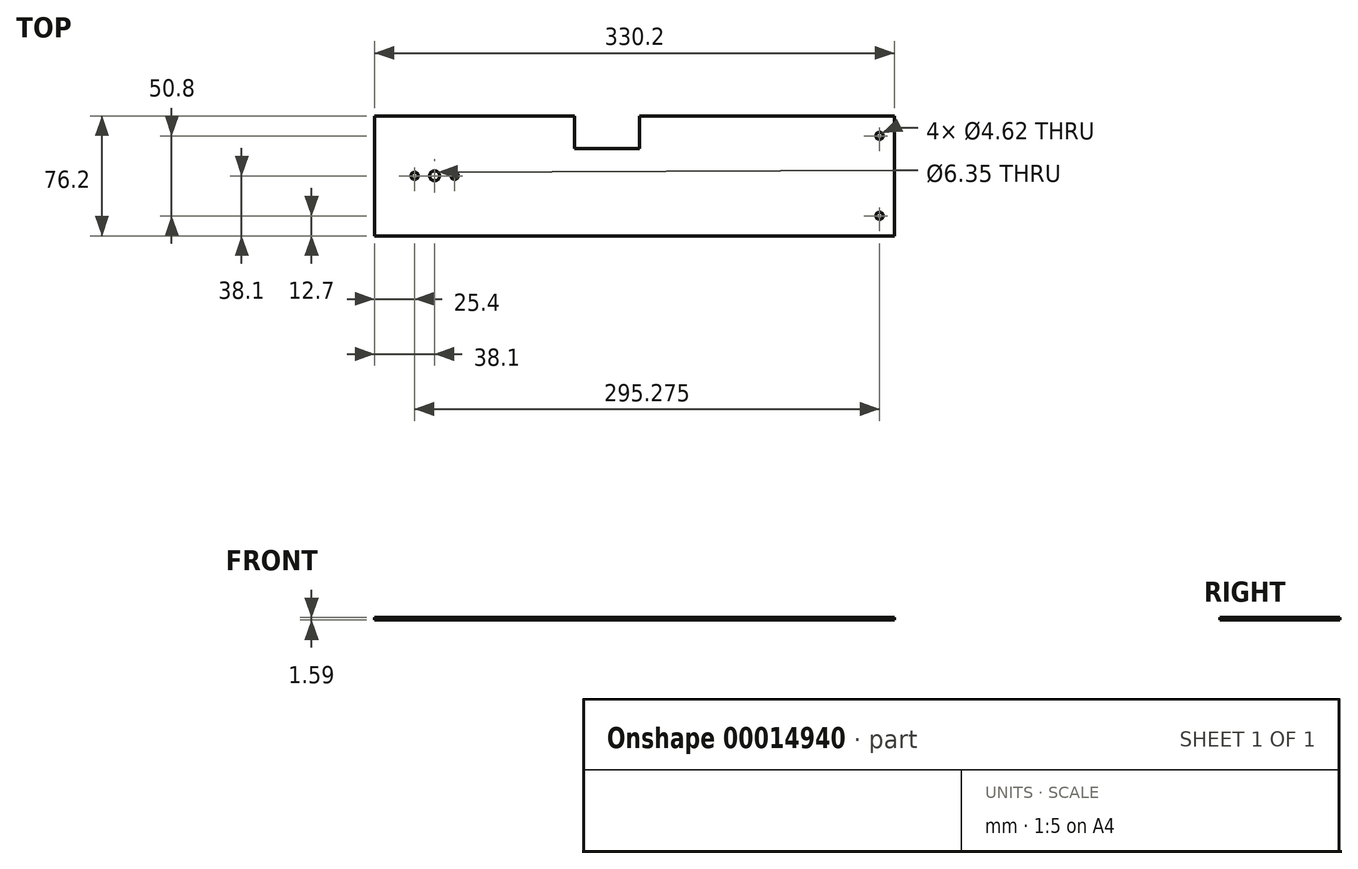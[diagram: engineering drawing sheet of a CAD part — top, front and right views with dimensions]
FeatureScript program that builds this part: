
annotation { "Feature Type Name" : "Feature", "Feature Type Description" : "" }
export const myFeature = defineFeature(function(context is Context, id is Id, definition is map)
    precondition{}
    {
        {
            var Q0;
            Q0=qCreatedBy(makeId("Top.planeOp"),FACE);
            var sketch = newSketch(context, id + "F0", { "sketchPlane" : qUnion([Q0])});
            skLineSegment(sketch, "E0.bottom", {"start": v(0, 76.2) * mm, "end": v(330.2, 76.2) * mm});
            skLineSegment(sketch, "E0.top", {"start": v(0, 0) * mm, "end": v(330.2, 0) * mm});
            skLineSegment(sketch, "E0.left", {"start": v(0, 76.2) * mm, "end": v(0, 0) * mm});
            skLineSegment(sketch, "E0.right", {"start": v(330.2, 76.2) * mm, "end": v(330.2, 0) * mm});
            skCircle(sketch, "E1", {"center": v(38.1, 38.1) * mm, "radius": 3.18 * mm});
            skCircle(sketch, "E2", {"center": v(320.68, 12.7) * mm, "radius": 2.31 * mm});
            skCircle(sketch, "E3", {"center": v(320.68, 63.5) * mm, "radius": 2.31 * mm});
            skCircle(sketch, "E4", {"center": v(50.8, 38.1) * mm, "radius": 2.31 * mm});
            skCircle(sketch, "E5", {"center": v(25.4, 38.1) * mm, "radius": 2.31 * mm});
            skLineSegment(sketch, "E6.bottom", {"start": v(127, 76.2) * mm, "end": v(168.28, 76.2) * mm});
            skLineSegment(sketch, "E6.top", {"start": v(127, 55.56) * mm, "end": v(168.27, 55.56) * mm});
            skLineSegment(sketch, "E6.left", {"start": v(127, 76.2) * mm, "end": v(127, 55.56) * mm});
            skLineSegment(sketch, "E6.right", {"start": v(168.28, 76.2) * mm, "end": v(168.28, 55.56) * mm});
            skPoint(sketch, "E7", {"position": v(127, 65.88) * mm});
            skSolve(sketch);
        }
        {
            var Q0;
            Q0=makeQuery(id+"F0.imprint","IMPRINT",FACE,{"disambiguationData":[TD([[makeQuery(id+"F0.imprint","IMPRINT",EDGE,{"derivedFrom":sQuery(id+"F0.wireOp",EDGE,"E0.bottom")}),-1.0]])]});
            extrude(context, id + "F1", {"entities" : qUnion([Q0]), "depth" : 1.59 * mm});
        }
    });
